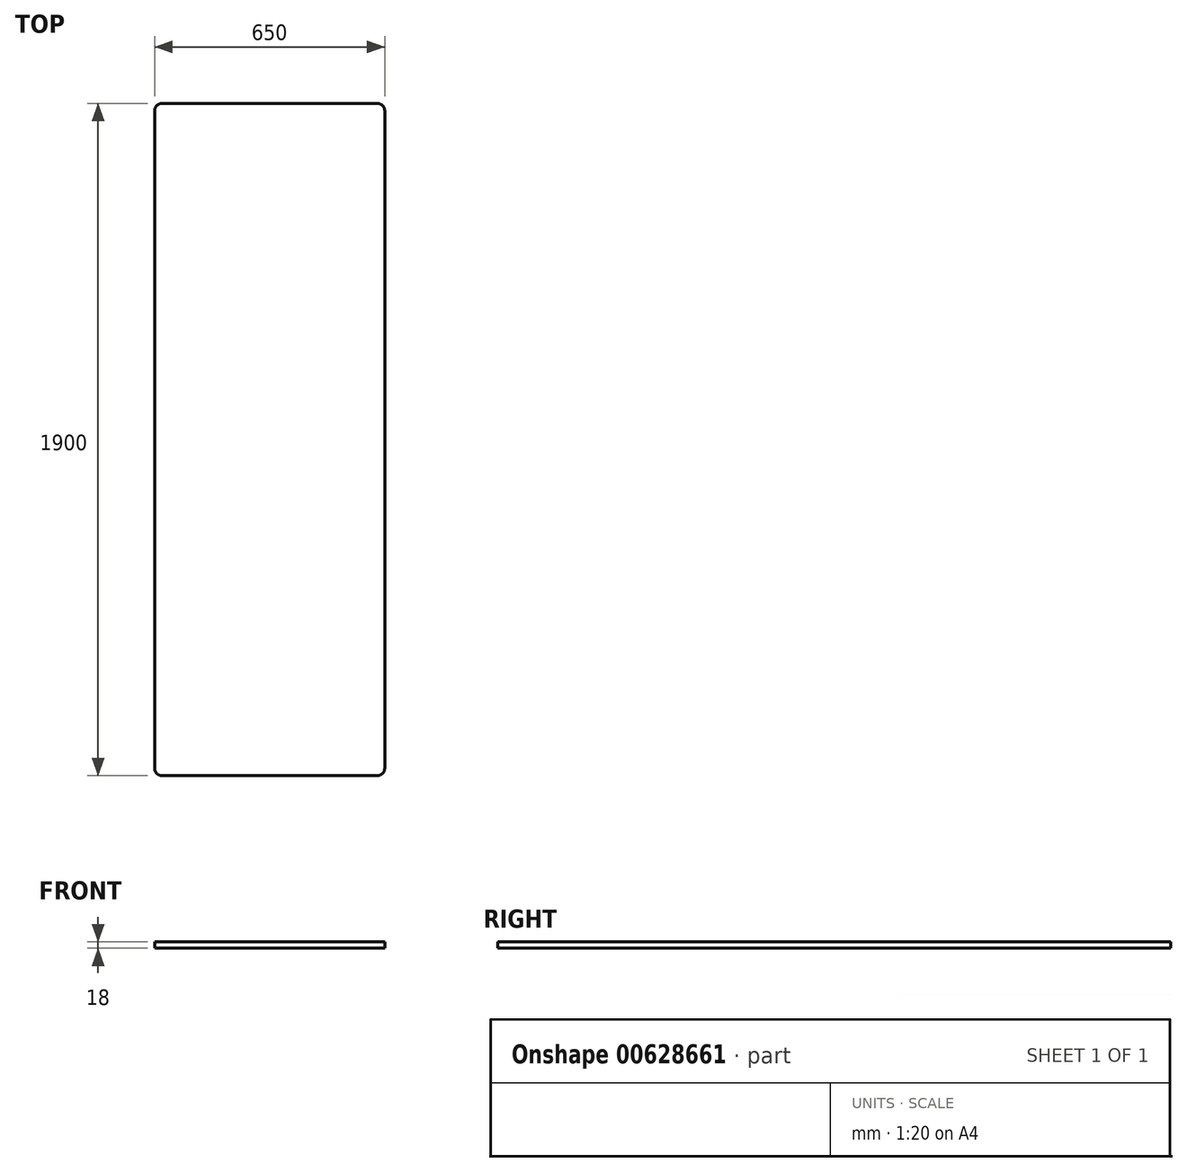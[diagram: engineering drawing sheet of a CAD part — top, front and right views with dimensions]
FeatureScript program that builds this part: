
annotation { "Feature Type Name" : "Feature", "Feature Type Description" : "" }
export const myFeature = defineFeature(function(context is Context, id is Id, definition is map)
    precondition{}
    {
        {
            var Q0;
            Q0=qCreatedBy(makeId("Front.planeOp"),FACE);
            var sketch = newSketch(context, id + "F0", { "sketchPlane" : qUnion([Q0])});
            skLineSegment(sketch, "E0.bottom", {"start": v(-325, 9) * mm, "end": v(325, 9) * mm});
            skLineSegment(sketch, "E0.top", {"start": v(-325, -9) * mm, "end": v(325, -9) * mm});
            skLineSegment(sketch, "E0.left", {"start": v(-325, 9) * mm, "end": v(-325, -9) * mm});
            skLineSegment(sketch, "E0.right", {"start": v(325, 9) * mm, "end": v(325, -9) * mm});
            skPoint(sketch, "E0.middle", {"position": v(0, 0) * mm});
            skSolve(sketch);
        }
        {
            var Q0;
            Q0=makeQuery(id+"F0.imprint","IMPRINT",FACE,{"disambiguationData":[TD([[makeQuery(id+"F0.imprint","IMPRINT",EDGE,{"derivedFrom":sQuery(id+"F0.wireOp",EDGE,"E0.bottom")}),-1.0]])]});
            extrude(context, id + "F1", {"entities" : qUnion([Q0]), "endBound" : BoundingType.SYMMETRIC, "depth" : 1900 * mm, "offsetDistance" : 25 * mm});
        }
        {
            var Q0;
            Q0=makeQuery(id+"F1.opExtrude","CAP_EDGE",EDGE,{"disambiguationData":[OSD([sQuery(id+"F0.wireOp",EDGE,"E0.left")])],"isStart":false});
            var Q1;
            Q1=makeQuery(id+"F1.opExtrude","CAP_EDGE",EDGE,{"disambiguationData":[OSD([sQuery(id+"F0.wireOp",EDGE,"E0.right")])],"isStart":false});
            var Q2;
            Q2=makeQuery(id+"F1.opExtrude","CAP_EDGE",EDGE,{"disambiguationData":[OSD([sQuery(id+"F0.wireOp",EDGE,"E0.right")])],"isStart":true});
            var Q3;
            Q3=makeQuery(id+"F1.opExtrude","CAP_EDGE",EDGE,{"disambiguationData":[OSD([sQuery(id+"F0.wireOp",EDGE,"E0.left")])],"isStart":true});
            fillet(context, id + "F2", {"entities" : qUnion([Q0, Q1, Q2, Q3]), "radius" : 20 * mm, "allowEdgeOverflow" : false});
        }
    });
